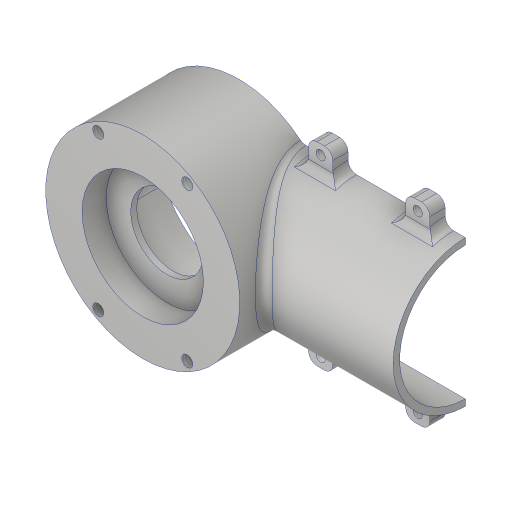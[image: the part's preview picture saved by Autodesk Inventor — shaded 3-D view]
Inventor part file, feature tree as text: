
AUTODESK INVENTOR PART (.ipt)
format: ipt  version: 2023.4 (Build 274418000, 418)  size: 790,528 bytes
history: native  units: in
note: dims shown in document units (in); Inventor stores cm internally (conversion verified against a paired STEP export)
features: sketch x26, extrude x16, projected_geometry x9, plane x8, hole x8, fillet x5, mirror x1, split x1
ambient origin geometry x8: Origin, YZ Plane, XZ Plane, XY Plane, X Axis, Y Axis, Z Axis, Center Point
bodies: Solid1 (feature_tree), Solid2 (feature_tree), Solid3 (feature_tree)
feature tree (74):
  extrude  "Extrusion1"  Depth=3.0in TaperAngle=0.0deg
  plane  "Work Plane1"
  extrude  "Extrusion2"  Depth=2.06in
  extrude  "Extrusion3"  Depth=3.0in TaperAngle=0.0deg
  hole  "Hole1"  [1 undecoded]
  plane  "Work Plane2"
  plane  "Work Plane3"
  extrude  "Extrusion5"  Depth=0.5in
  hole  "Hole2"  [1 undecoded]
  plane  "Work Plane8"
  extrude  "Extrusion14"  Depth=1.375in
  extrude  "Extrusion6"  Depth=0.13in
  hole  "Hole3"  [1 undecoded]
  fillet  "Fillet4"  Radius=1.0in
  mirror  "Mirror2"
  hole  "Hole5"  [1 undecoded]
  sketch  "Sketch14"  dims[d45=2.375in]
  plane  "Work Plane4"
  extrude  "Extrusion8"  Depth=1.5in
  fillet  "Fillet5"  Radius=0.5in
  plane  "Work Plane5"
  extrude  "Extrusion9"  Depth=1.5in TaperAngle=0.0deg
  plane  "Work Plane6"
  extrude  "Extrusion10"  Depth=0.375in
  fillet  "Fillet6"  Radius=0.5in
  hole  "Hole6"  [1 undecoded]
  plane  "Work Plane7"
  extrude  "Extrusion11"  Depth=1.5in
  split  "Split1"
  extrude  "Extrusion12"  [1 undecoded]
  extrude  "Extrusion13"  Depth=0.125in TaperAngle=0.0deg
  sketch  "Sketch23"  dims[d97=0.13in]
  extrude  "Extrusion15"  Depth=0.015in TaperAngle=0.0deg
  sketch  "Sketch25"  dims[d106=0.1in d107=0.125in d108=0.0in]
  extrude  "Extrusion16"  Depth=0.125in
  fillet  "Fillet7"  Radius=0.125in
  hole  "Hole8"  [1 undecoded]
  hole  "Hole9"  [1 undecoded]
  extrude  "Extrusion17"  TaperAngle=0.0deg  [1 undecoded]
  extrude  "Extrusion18"  Depth=0.25in
  fillet  "Fillet8"  Radius=1.25in
  hole  "Hole10"  [1 undecoded]
  sketch  "Sketch1"  dims[d0=3.0in d1=3.0in d2=0.0in]
  sketch  "Sketch2"  dims[d3=3.5in d4=2.06in]
  sketch  "Sketch3"  dims[d5=0.1in d6=3.0in d7=0.0in]
  sketch  "Sketch4"  dims[d8=3.3in d9=0.0in]
  sketch  "Sketch7"  dims[d11=1.125in d12=0.75in d13=1.875in d14=0.375in d15=0.5635in d16=1.625in d17=0.8108in d22=1.5in d27=-1.875in]
  sketch  "Sketch8"  dims[d28=0.375in d29=0.5in]
  sketch  "Sketch9"  dims[d30=1.0in d31=0.0in]
  sketch  "Sketch10"  dims[d34=1.125in d35=0.75in d36=1.875in d37=0.375in d38=0.5635in d39=1.0in d40=0.8108in d41=2.0625in d42=0.0in]
  sketch  "Sketch13"  dims[d43=2.744in d44=1.375in]
  sketch  "Sketch15"  dims[d46=0.171in d47=0.432in d48=0.385in d49=0.25in d50=0.5635in d51=1.0in d52=0.8108in d69=0.13in]
  sketch  "Sketch16"  dims[d70=0.156in d71=0.38in d72=0.375in d73=0.25in d74=0.5635in d75=1.0in d76=0.8108in d77=45.0deg d78=1.0in]
  sketch  "Sketch17"  dims[d79=1.0in d80=0.0in d81=0.02in]
  sketch  "Sketch18"  dims[d83=1.5in d84=0.375in d85=0.5in]
  sketch  "Sketch19"  dims[d86=1.5in d87=0.5in d88=0.0in]
  sketch  "Sketch20"  dims[d89=-1.5in d90=0.375in d91=0.5in]
  sketch  "Sketch21"  dims[d92=1.5in d93=0.5in d94=0.0in]
  sketch  "Sketch22"  dims[d95=1.5in d96=1.5in]
  sketch  "Sketch24"  dims[d98=0.145in d99=0.38in d100=0.385in d101=0.25in d102=0.5635in d103=1.0in d104=0.8108in d105=-2.0in]
  sketch  "Sketch26"  dims[d109=0.015in d110=0.0in d111=0.015in d112=0.0in]
  sketch  "Sketch27"  dims[d113=-1.875in d114=0.125in d115=0.125in d116=0.0in]
  sketch  "Sketch28"  dims[d117=0.0in d118=0.0in d126=1.25in]
  sketch  "Sketch29"  dims[d127=1.0in d128=0.0in d129=0.26in]
  sketch  "Sketch30"  dims[d130=0.156in d131=0.38in d132=0.313in d133=0.164in d134=0.5635in d135=0.536in d136=0.0in d137=0.313in d138=0.38in d139=0.375in d140=0.25in d141=0.5635in d142=0.201in d143=0.0in d144=0.0in d145=0.0in d146=0.5in d147=1.25in d148=0.5in d149=1.25in d150=1.0in d151=0.0in d152=0.26in d153=0.156in d154=0.5in d155=0.375in d156=0.25in d157=0.5635in d158=0.75in d159=0.8108in]
  projected_geometry  "Project Cut Edges3"
  projected_geometry  "Project Cut Edges4"
  projected_geometry  "Project Cut Edges5"
  projected_geometry  "Project Cut Edges6"
  projected_geometry  "Project Cut Edges7"
  projected_geometry  "Project Cut Edges8"
  projected_geometry  "Project Cut Edges9"
  projected_geometry  "Project Cut Edges10"
  projected_geometry  "Project Cut Edges11"
note: 10 required parameter values undecoded (feature->parameter linkage not recoverable at this tier; creation-order binding heuristic only, values carry confidence <= 0.55)
